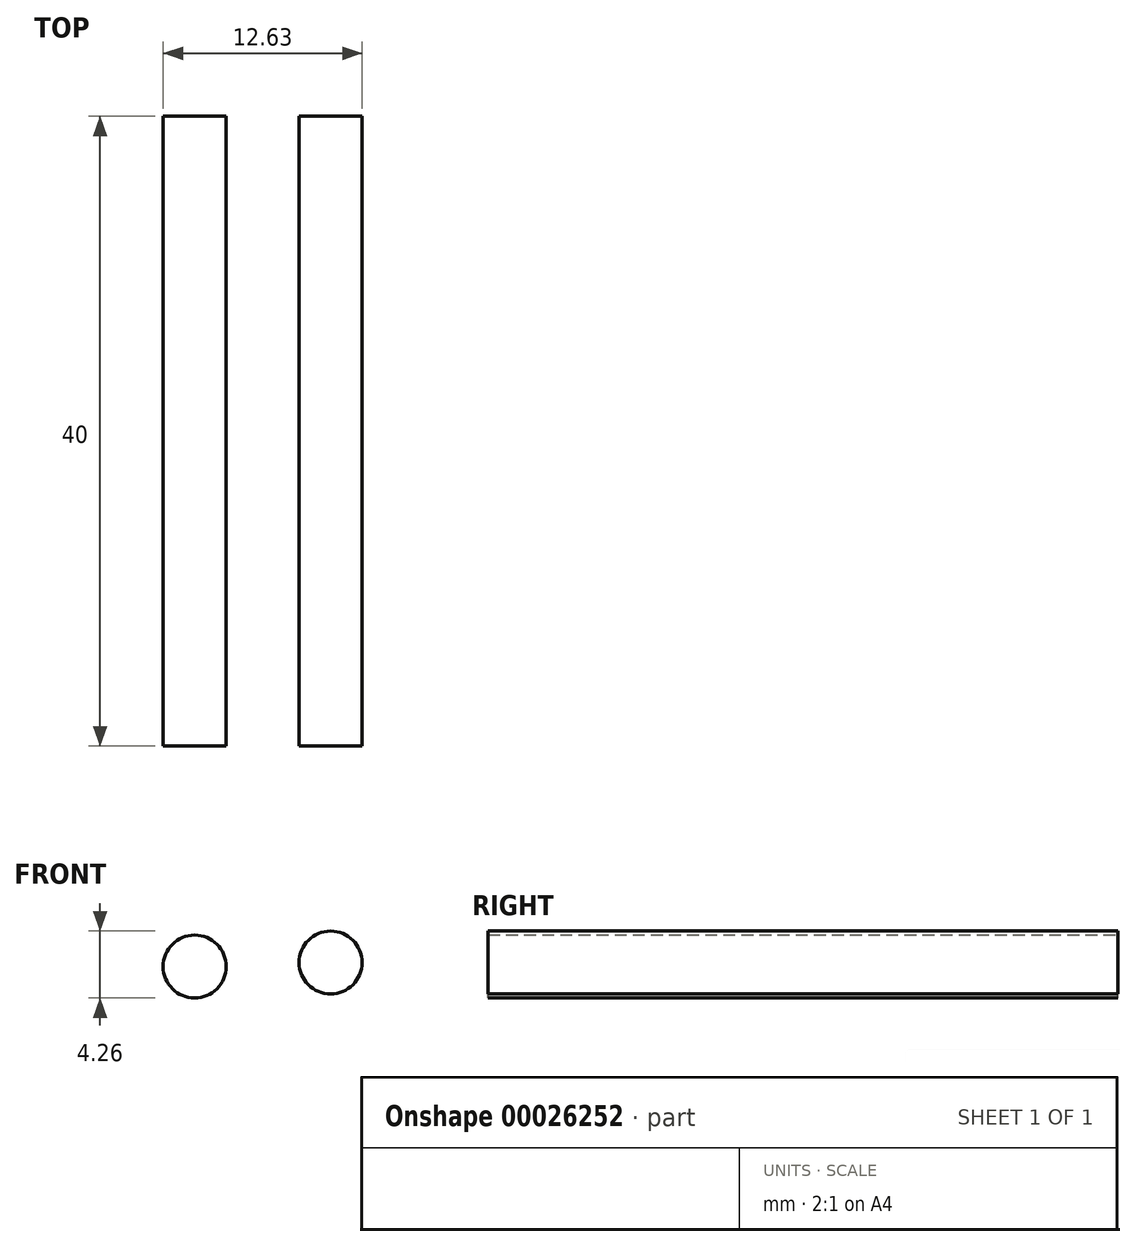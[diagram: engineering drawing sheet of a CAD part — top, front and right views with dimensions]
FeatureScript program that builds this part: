
annotation { "Feature Type Name" : "Feature", "Feature Type Description" : "" }
export const myFeature = defineFeature(function(context is Context, id is Id, definition is map)
    precondition{}
    {
        {
            var Q0;
            Q0=qCreatedBy(makeId("Front.planeOp"),FACE);
            var sketch = newSketch(context, id + "F0", { "sketchPlane" : qUnion([Q0])});
            skCircle(sketch, "E0", {"center": v(-16.03, 36.32) * mm, "radius": 2 * mm});
            skCircle(sketch, "E1", {"center": v(-7.4, 36.58) * mm, "radius": 2 * mm});
            skSolve(sketch);
        }
        {
            var Q0;
            Q0 = qSketchRegion(id + "F0", true);
            extrude(context, id + "F1", {"entities" : qUnion([Q0]), "depth" : 40 * mm});
        }
    });
